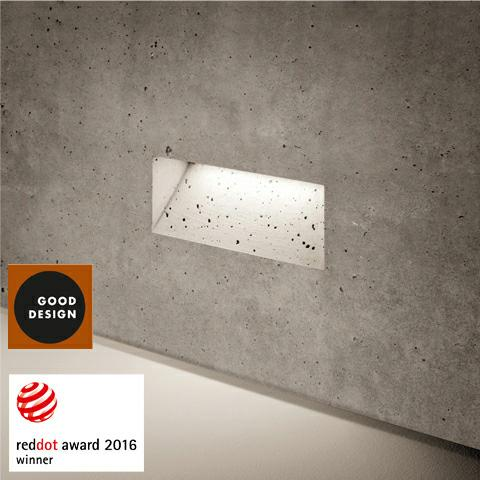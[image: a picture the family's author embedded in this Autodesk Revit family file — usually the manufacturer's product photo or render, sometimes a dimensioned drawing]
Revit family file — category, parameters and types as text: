
# Revit family: SIMES_C.8022W_Ghost
name_source: partatom
category: Lighting Fixtures
revit_build: Autodesk Revit 2016 (Build: 20150714_1515(x64)
units: mm (PartAtom-declared; Revit-internal decimal feet)

## family parameters
Cut with Voids When Loaded = No
Host = Face
Light Source = Yes
OmniClass Number = 23.80.70.14
OmniClass Title = Luminaries for External Lighting
Part Type = Normal
Room Calculation Point = No
Round Connector Dimension = Use Diameter
Shared = No

## types (1)
- SIMES_C.8022W_Ghost
    Approval mark = CE
    Assembly Code = D5020
    Color Filter = 16777215
    Color Rendering Index = CRI 80
    Colour Temperature = 3000
    Control Gear = electronic transformer
    Default Elevation = 1219 mm
    Description = GHOST HORIZONTAL
Art. C.8022W
MODULES LED 3000K  230V CRI 80
Rated luminaire luminous flux: 490lm
Rated input power: 10W
Luminaire efficacy: 49lm/W
Electronic ballast 220÷230V 50-60Hz
CE

PRODUCT TYPE
Wall mounted luminaire. IP rating IP 65
MATERIAL CHARACTERISTICS
Ghost is a lighting void that is obtained from a polypropylene housing anchored to the retaining panels before pouring the concrete. Ghost is composed of two elements: the housing and the lighting element. The housing is in polypropylene and it consists of two complementary parts: - A jig , which forms the housing, and is extracted together with the retaining panel after completing the casting and removing the anchor screws; - The housing  that remains embedded inside the casting and houses the lighting element. (The housing is supplied with bolts, locking system and stickers to be applied on the outside of the retaining panels so to secure a perfect alignment for multiple installations of each housing when pouring the concrete). The lighting element in die cast aluminum is anchored to the casing  through proper screws and it remains completely hided into the void. Mechanical resistance IK 06
MAINTENANCE
This product is manufactured on site during the concrete casting of the wall with hand crafted procedures; therefore, small imperfections caused by the low accurance of the casting, subsidence of the concrete surface, actual and future cracks, colour ripples and variations over time, will be deliberately present and they are a feature of the concrete, proving the hand-made manufacturing procedure.
LIGHTING PERFORMANCE
Toughened glass diffuser. LOR -- 
WIRING
Supplied with a pre-wired 0.3m H05RN-F cable. Isolation: CLASS I . Available colours: Cast cement. Weight: 1.3 Kg Glow Wire test: --
L.E.D circuit included.
GHOST PATENDED, REGISTERED DESIGN
This luminaire contains built-in LED modules with energy class: A, A+, A++. In case of damage or malfunction please contact the manufacturer to receive additional instructions on how to replace and relative spare parts to order. The LED modules cannot be handled in the luminaire by the end user (Regulation UE 874/2012).
LED circuit boards are engineered accordingly to actual Lumen Maintenance regulation (LM80) and Technical Memorandum (TM21) where uniformity and quality of light is 50.000 hours referred to L70  B20 Ta 25°C.Lifecycle refers to LED circuit boards only, all others components of the luminaire are excluded.
    Dimming Lamp Color Temperature Shift = <None>
    Frequency = 50-60Hz
    IFC Classification = Light Fixture
    IK Rating = IK 06
    Lamp = LED
    Lamp Light Flux = 880
    Lamp Power = 10
    Lamp count = 1
    Last Update = 02/08/2018 10:21:19
    Lifetime = 50000 L70 B20 Ta 25°C
    Light Output Ratio = 100
    Luminous efficacy = 49
    Manufacturer = SIMES
    Masterformat 2014 Code = 26 56 00
    Masterformat 2014 Description = Exterior Lighting
    Model = C.8022W
    Mounting Place = Wall
    Mounting Type = Recessed
    NBS Reference Code = 49
    NBS Reference Description = Luminaries And Lamps
    OmniClass Code = 23-35 47 11
    OmniClass Description = Lighting Fixture
    Photometric Web File = C8022W.ies
    Product Group = recessed luminaire
    Product Name = Ghost for cast concrete
    Protection Class = Protection class I
    Protection Degree = IP 65
    System Light Flux = 490
    System Power = 10
    Tilt Angle = -180.00°
    Type Comments = SIMES S.p.A. - All rights reserved
    Type Image = Ghost rettangolare.jpg
    UNSPSC Code = 3911
    URL = http://www.simes.it
    Uniclass 1.4 Code = YJ73
    Uniclass 1.4 Description = Luminaries and lamps
    Uniclass 2.0 Code = PR-49
    Uniclass 2.0 Description = Luminaries and lamps
    Uniclass 2015 Code = EF_70_80
    Uniclass 2015 Name = Lighting
    Uniformat II Code = D5020
    Uniformat II Description = Lighting & Branch Wiring
    Voltage = 220÷230V
    Wattage Comments = 9.5W
